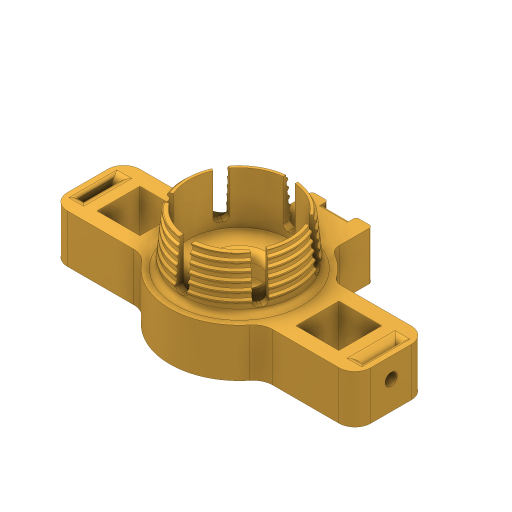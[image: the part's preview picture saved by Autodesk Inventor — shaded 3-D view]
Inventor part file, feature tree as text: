
AUTODESK INVENTOR PART (.ipt)
format: ipt  version: 2023 (Build 270158000, 158)  size: 1,379,840 bytes
history: native  units: mm
features: fillet x10, sketch x8, extrude x6, hole x3, helix x2, direct_edit x2, draft x1, plane x1, mirror x1, other x1, revolve x1
ambient origin geometry x8: Origin, YZ Plane, XZ Plane, XY Plane, X Axis, Y Axis, Z Axis, Center Point
bodies: Solid1 (feature_tree)
feature tree (36):
  extrude  "Extrusion1"  Depth=26.5mm
  draft  "FaceDraft1"
  sketch  "Sketch2"  dims[d34=0.0mm d35=0.0mm d56=8.726646mm]
  helix  "Coil3"  [1 undecoded]
  helix  "Coil4"  [1 undecoded]
  direct_edit  "Direct Edit2"
  extrude  "Extrusion2"  Depth=8.726646mm
  extrude  "Extrusion13"  TaperAngle=90.0deg  [1 undecoded]
  plane  "Work Plane5"
  extrude  "Extrusion14"  Depth=34.58632mm
  hole  "Hole3"  [1 undecoded]
  hole  "Hole4"  [1 undecoded]
  fillet  "Fillet11"  Radius=60.0mm
  fillet  "Fillet22"  [1 undecoded]
  hole  "Hole6"  [1 undecoded]
  mirror  "Mirror3"
  extrude  "Extrusion15"  Depth=0.75mm
  direct_edit  "Direct Edit3"
  fillet  "Fillet15"  Radius=18.0mm
  fillet  "Fillet16"  Radius=10.65mm
  fillet  "Fillet17"  Radius=10.0mm
  fillet  "Fillet18"  Radius=15.0mm
  fillet  "Fillet19"  Radius=10.0mm
  fillet  "Fillet20"  Radius=7.0mm
  fillet  "Fillet21"  Radius=10.0mm
  extrude  "Extrusion16"  Depth=0.75mm TaperAngle=0.0deg
  fillet  "Fillet24"  [1 undecoded]
  sketch  "Sketch1"  dims[d0=25.0mm d1=26.5mm d2=12.875mm d3=0.0mm d4=1.047198mm]
  sketch  "Sketch3"  dims[d62=2.0mm d63=10.15mm d64=10.0mm d65=1.047198mm]
  sketch  "Sketch13"  dims[d66=90.0deg d67=90.0deg d68=0.0mm d69=0.0mm d70=2.0mm d71=3.0mm d72=10.0mm d73=-1.047198mm d74=90.0deg d75=90.0deg d76=0.0mm d77=0.0mm]
  sketch  "Sketch14"  dims[d79=-0.127mm d145=34.58632mm]
  sketch  "Sketch16"  dims[d150=120.0deg d151=120.0deg]
  sketch  "Sketch17"  dims[d153=21.6866mm d157=12.0mm d158=0.0mm d160=60.0mm d162=360.0deg d164=0.0mm d165=0.0mm]
  sketch  "Sketch18"  dims[d179=5.3mm d180=6.0mm d181=4.0mm d182=2.0mm d183=90.0deg d184=5.0mm d185=0.0mm d186=10.0mm d187=6.0mm d188=4.0mm d189=2.0mm d190=90.0deg d191=7.0mm d192=0.0mm d193=2.0mm d194=20.0mm d195=18.0mm d196=10.65mm d197=10.0mm d206=15.0mm d207=10.0mm d208=7.0mm d209=10.0mm d210=1.0mm d211=0.0mm d212=-4.363323mm d215=1.5mm d216=3.0mm d217=8.0mm d219=1.0mm d220=5.0mm d221=3.0mm d222=6.0mm d223=4.0mm d224=2.0mm d225=90.0deg d226=6.5mm d227=0.0mm d228=3.0mm d229=5.0mm d230=4.0mm d234=2.0mm d235=0.7mm d237=1.5mm d238=1.2mm d239=1.3mm d241=0.0mm d242=0.0mm d243=0.75mm d109=0.5mm d110=0.872665mm d111=0.5mm d112=0.872665mm d236=0.5mm]
  other  "Size2"
  revolve  "Rotate1"  [1 undecoded]
note: 9 required parameter values undecoded (feature->parameter linkage not recoverable at this tier; creation-order binding heuristic only, values carry confidence <= 0.55)